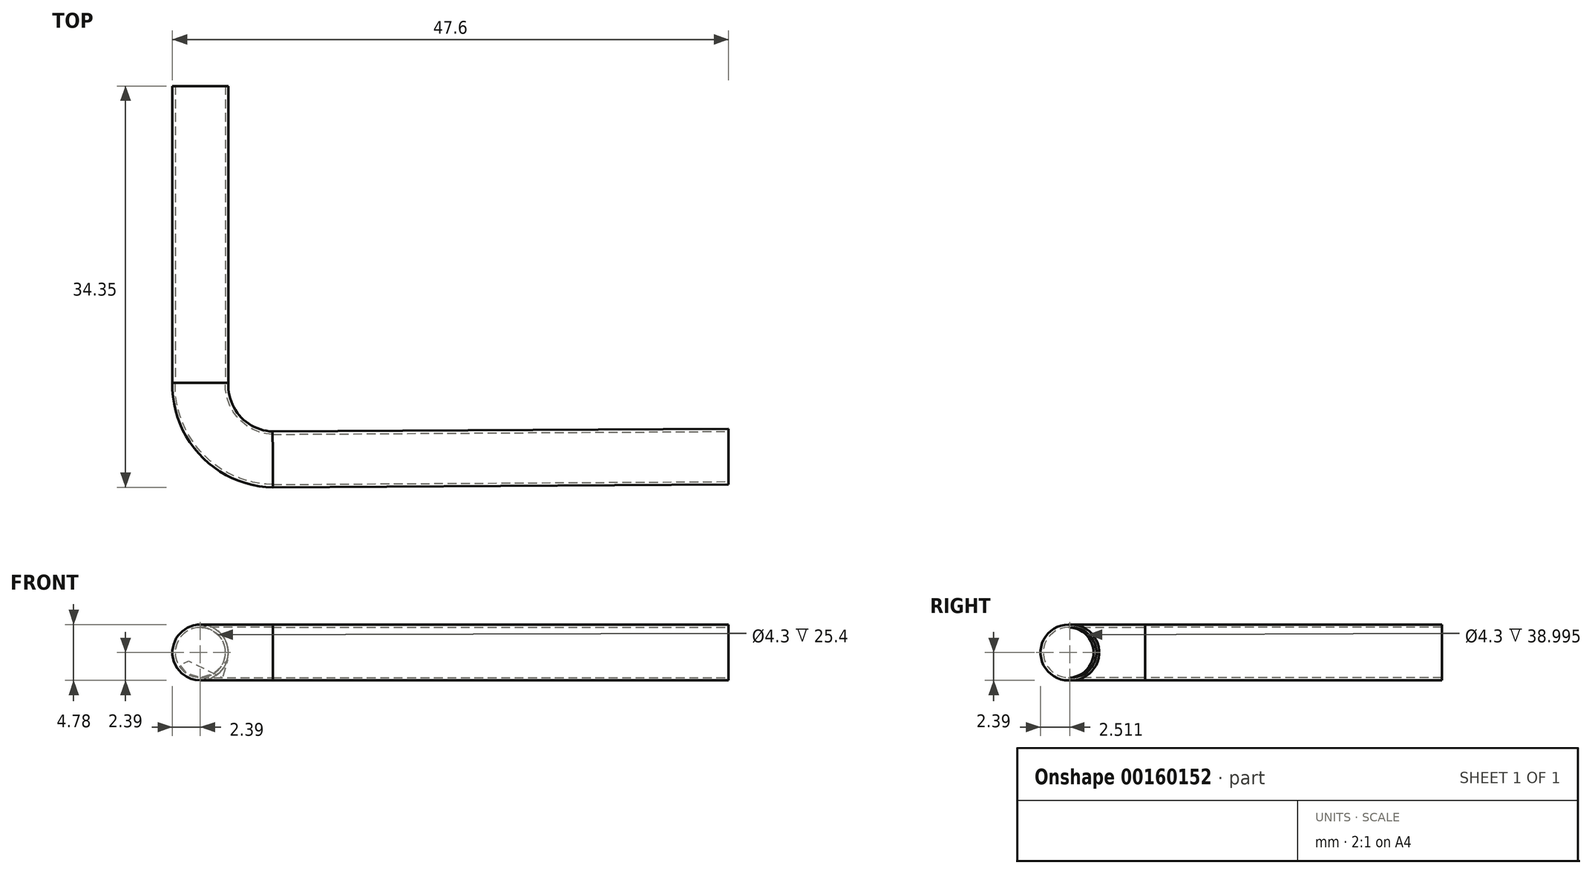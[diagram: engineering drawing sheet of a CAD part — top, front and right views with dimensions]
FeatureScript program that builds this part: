
annotation { "Feature Type Name" : "Feature", "Feature Type Description" : "" }
export const myFeature = defineFeature(function(context is Context, id is Id, definition is map)
    precondition{}
    {
        {
            var Q0;
            Q0=qCreatedBy(makeId("Front.planeOp"),FACE);
            var sketch = newSketch(context, id + "F0", { "sketchPlane" : qUnion([Q0])});
            skCircle(sketch, "E0", {"center": v(0, 0) * mm, "radius": 2.39 * mm});
            skSolve(sketch);
        }
        {
            var Q0;
            Q0 = qSketchRegion(id + "F0", true);
            extrude(context, id + "F1", {"entities" : qUnion([Q0]), "depth" : 19.05 * mm});
        }
        {
            var Q0;
            Q0=qCreatedBy(makeId("Front.planeOp"),FACE);
            var sketch = newSketch(context, id + "F2", { "sketchPlane" : qUnion([Q0])});
            skCircle(sketch, "E1", {"center": v(0, 0) * mm, "radius": 2.04 * mm});
            skSolve(sketch);
        }
        {
            var Q0;
            Q0 = qSketchRegion(id + "F2", true);
            extrude(context, id + "F3", {"entities" : qUnion([Q0]), "operationType" : NewBodyOperationType.REMOVE, "endBound" : BoundingType.THROUGH_ALL, "oppositeDirection" : true, "depth" : 25.4 * mm});
        }
        {
            var Q0;
            Q0=makeQuery(id+"F1.opExtrude","CAP_FACE",FACE,{"disambiguationData":[OSD([sQuery(id+"F0.wireOp",EDGE,"E0")])],"isStart":false});
            var sketch = newSketch(context, id + "F4", { "sketchPlane" : qUnion([Q0])});
            skCircle(sketch, "E2", {"center": v(0, 0) * mm, "radius": 2.15 * mm});
            skSolve(sketch);
        }
        {
            var Q0;
            Q0 = qSketchRegion(id + "F4", true);
            extrude(context, id + "F5", {"entities" : qUnion([Q0]), "operationType" : NewBodyOperationType.REMOVE, "endBound" : BoundingType.THROUGH_ALL, "oppositeDirection" : true, "depth" : 25.4 * mm});
        }
        {
            var Q0;
            Q0=qCreatedBy(makeId("Top.planeOp"),FACE);
            var sketch = newSketch(context, id + "F6", { "sketchPlane" : qUnion([Q0])});
            skPoint(sketch, "E3.startSnap0", {"position": v(0.36, 0) * mm});
            skLineSegment(sketch, "E4", {"start": v(0.36, 0) * mm, "end": v(0, 0) * mm, "construction": true});
            skLineSegment(sketch, "E5", {"start": v(0, -19.25) * mm, "end": v(0, -25.6) * mm});
            skArc(sketch, "E6", {"start": v(0, -25.6) * mm, "mid": v(1.88, -30.11) * mm, "end": v(6.4, -31.96) * mm});
            skLineSegment(sketch, "E7", {"start": v(6.4, -31.96) * mm, "end": v(45.4, -31.71) * mm});
            skSolve(sketch);
        }
        {
            var Q0;
            Q0=makeQuery(id+"F1.opExtrude","CAP_FACE",FACE,{"disambiguationData":[OSD([sQuery(id+"F0.wireOp",EDGE,"E0")])],"isStart":false});
            var Q1;
            Q1=sQuery(id+"F6.wireOp",EDGE,"E5");
            var Q2;
            Q2=sQuery(id+"F6.wireOp",EDGE,"E6");
            var Q3;
            Q3=sQuery(id+"F6.wireOp",EDGE,"E7");
            sweep(context, id + "F7", {"operationType" : NewBodyOperationType.ADD, "profiles" : qUnion([Q0]), "path" : qUnion([Q1, Q2, Q3])});
        }
    });
